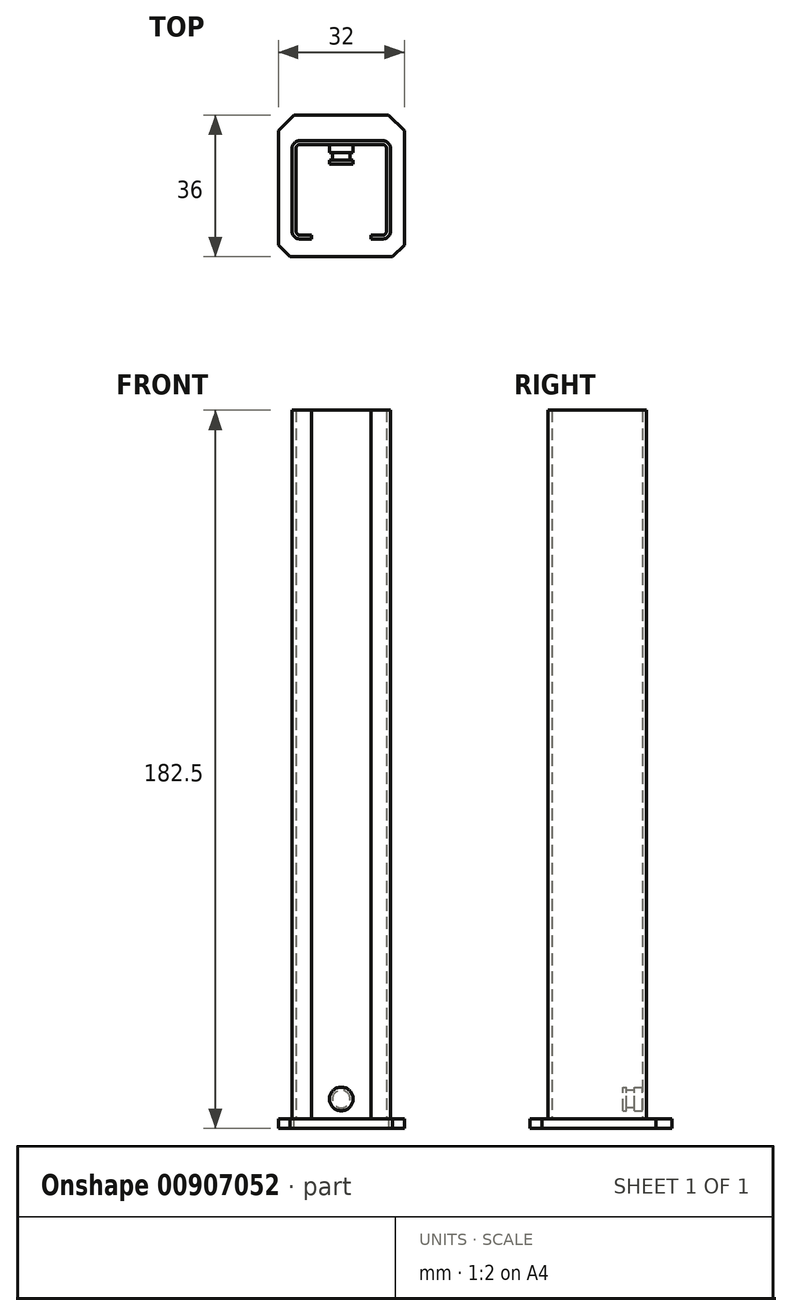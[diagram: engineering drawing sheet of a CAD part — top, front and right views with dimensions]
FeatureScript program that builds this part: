
annotation { "Feature Type Name" : "Feature", "Feature Type Description" : "" }
export const myFeature = defineFeature(function(context is Context, id is Id, definition is map)
    precondition{}
    {
        {
            var Q0;
            Q0=qCreatedBy(makeId("Top.planeOp"),FACE);
            var sketch = newSketch(context, id + "F0", { "sketchPlane" : qUnion([Q0])});
            skLineSegment(sketch, "E0.bottom", {"start": v(16, 19) * mm, "end": v(-16, 19) * mm});
            skLineSegment(sketch, "E0.top", {"start": v(16, -17) * mm, "end": v(-16, -17) * mm});
            skLineSegment(sketch, "E0.left", {"start": v(16, 19) * mm, "end": v(16, -17) * mm});
            skLineSegment(sketch, "E0.right", {"start": v(-16, 19) * mm, "end": v(-16, -17) * mm});
            skPoint(sketch, "E0.middle", {"position": v(0, 1) * mm});
            skSolve(sketch);
        }
        {
            var Q0;
            Q0 = qSketchRegion(id + "F0", true);
            extrude(context, id + "F1", {"entities" : qUnion([Q0]), "oppositeDirection" : true, "depth" : 2.5 * mm, "offsetDistance" : 25.4 * mm});
        }
        {
            var Q0;
            Q0=makeQuery(id+"F1.opExtrude","CAP_FACE",FACE,{"disambiguationData":[OSD([sQuery(id+"F0.wireOp",EDGE,"E0.bottom"),sQuery(id+"F0.wireOp",EDGE,"E0.top"),sQuery(id+"F0.wireOp",EDGE,"E0.left"),sQuery(id+"F0.wireOp",EDGE,"E0.right")])],"isStart":true});
            var sketch = newSketch(context, id + "F2", { "sketchPlane" : qUnion([Q0])});
            skLineSegment(sketch, "E1.bottom", {"start": v(12.5, 12.5) * mm, "end": v(-12.5, 12.5) * mm});
            skLineSegment(sketch, "E1.top", {"start": v(12.5, -12.5) * mm, "end": v(7.5, -12.5) * mm});
            skLineSegment(sketch, "E1.left", {"start": v(12.5, 12.5) * mm, "end": v(12.5, -12.5) * mm});
            skLineSegment(sketch, "E1.right", {"start": v(-12.5, 12.5) * mm, "end": v(-12.5, -12.5) * mm});
            skPoint(sketch, "E1.middle", {"position": v(0, 0) * mm});
            skLineSegment(sketch, "E2.0", {"start": v(11.5, 11.5) * mm, "end": v(-11.5, 11.5) * mm});
            skLineSegment(sketch, "E2.1", {"start": v(11.5, 11.5) * mm, "end": v(11.5, -11.5) * mm});
            skLineSegment(sketch, "E2.2", {"start": v(11.5, -11.5) * mm, "end": v(7.5, -11.5) * mm});
            skLineSegment(sketch, "E2.3", {"start": v(-11.5, 11.5) * mm, "end": v(-11.5, -11.5) * mm});
            skLineSegment(sketch, "E3", {"start": v(-7.5, -11.5) * mm, "end": v(-7.5, -12.5) * mm});
            skLineSegment(sketch, "E4.MirrorCS", {"start": v(7.5, -11.5) * mm, "end": v(7.5, -12.5) * mm});
            skLineSegment(sketch, "E5.trimOffspring", {"start": v(-7.5, -11.5) * mm, "end": v(-11.5, -11.5) * mm});
            skLineSegment(sketch, "E6.trimOffspring", {"start": v(-7.5, -12.5) * mm, "end": v(-12.5, -12.5) * mm});
            skSolve(sketch);
        }
        {
            var Q0;
            Q0 = qSketchRegion(id + "F2", true);
            extrude(context, id + "F3", {"entities" : qUnion([Q0]), "operationType" : NewBodyOperationType.ADD, "depth" : 180 * mm, "offsetDistance" : 25 * mm});
        }
        {
            var Q0;
            Q0=makeQuery(id+"F3.opExtrude","SWEPT_EDGE",EDGE,{"disambiguationData":[OSD([sQuery(id+"F2.wireOp",EDGE,"E2.0"),sQuery(id+"F2.wireOp",EDGE,"E2.3")])]});
            var Q1;
            Q1=makeQuery(id+"F3.opExtrude","SWEPT_EDGE",EDGE,{"disambiguationData":[OSD([sQuery(id+"F2.wireOp",EDGE,"E2.0"),sQuery(id+"F2.wireOp",EDGE,"E2.1")])]});
            var Q2;
            Q2=makeQuery(id+"F3.opExtrude","SWEPT_EDGE",EDGE,{"disambiguationData":[OSD([sQuery(id+"F2.wireOp",EDGE,"E2.3"),sQuery(id+"F2.wireOp",EDGE,"E5.trimOffspring")])]});
            var Q3;
            Q3=makeQuery(id+"F3.opExtrude","SWEPT_EDGE",EDGE,{"disambiguationData":[OSD([sQuery(id+"F2.wireOp",EDGE,"E2.1"),sQuery(id+"F2.wireOp",EDGE,"E2.2")])]});
            fillet(context, id + "F4", {"entities" : qUnion([Q0, Q1, Q2, Q3]), "radius" : 1 * mm, "tangentPropagation" : true, "allowEdgeOverflow" : false});
        }
        {
            var Q0;
            Q0=makeQuery(id+"F3.opExtrude","SWEPT_EDGE",EDGE,{"disambiguationData":[OSD([sQuery(id+"F2.wireOp",EDGE,"E1.bottom"),sQuery(id+"F2.wireOp",EDGE,"E1.right")])]});
            var Q1;
            Q1=makeQuery(id+"F3.opExtrude","SWEPT_EDGE",EDGE,{"disambiguationData":[OSD([sQuery(id+"F2.wireOp",EDGE,"E1.bottom"),sQuery(id+"F2.wireOp",EDGE,"E1.left")])]});
            var Q2;
            Q2=makeQuery(id+"F3.opExtrude","SWEPT_EDGE",EDGE,{"disambiguationData":[OSD([sQuery(id+"F2.wireOp",EDGE,"E1.top"),sQuery(id+"F2.wireOp",EDGE,"E1.left")])]});
            var Q3;
            Q3=makeQuery(id+"F3.opExtrude","SWEPT_EDGE",EDGE,{"disambiguationData":[OSD([sQuery(id+"F2.wireOp",EDGE,"E1.right"),sQuery(id+"F2.wireOp",EDGE,"E6.trimOffspring")])]});
            fillet(context, id + "F5", {"entities" : qUnion([Q0, Q1, Q2, Q3]), "radius" : 2 * mm, "tangentPropagation" : true, "allowEdgeOverflow" : false});
        }
        {
            var Q0;
            Q0=makeQuery(id+"F3.opExtrude","SWEPT_FACE",FACE,{"disambiguationData":[OSD([sQuery(id+"F2.wireOp",EDGE,"E2.0")])]});
            var sketch = newSketch(context, id + "F6", { "sketchPlane" : qUnion([Q0])});
            skCircle(sketch, "E7", {"center": v(0, 5) * mm, "radius": 3 * mm});
            skSolve(sketch);
        }
        {
            var Q0;
            Q0 = qSketchRegion(id + "F6", true);
            extrude(context, id + "F7", {"entities" : qUnion([Q0]), "operationType" : NewBodyOperationType.ADD, "depth" : 5 * mm, "offsetDistance" : 25 * mm});
        }
        {
            var Q0;
            Q0=makeQuery(id+"F3.opExtrude","SWEPT_FACE",FACE,{"disambiguationData":[OSD([sQuery(id+"F2.wireOp",EDGE,"E2.0")])]});
            cPlane(context, id + "F8", {"entities" : qUnion([Q0]), "cplaneType" : CPlaneType.OFFSET, "offset" : 3 * mm, "width" : 150 * mm, "height" : 150 * mm});
        }
        {
            var Q0;
            Q0=qCreatedBy(id+"F8.planeOp",FACE);
            var sketch = newSketch(context, id + "F9", { "sketchPlane" : qUnion([Q0])});
            skCircle(sketch, "E8.0", {"center": v(0, 5) * mm, "radius": 3 * mm});
            skCircle(sketch, "E9", {"center": v(0, 5) * mm, "radius": 2.25 * mm});
            skSolve(sketch);
        }
        {
            var Q0;
            Q0 = qSketchRegion(id + "F9", true);
            extrude(context, id + "F10", {"entities" : qUnion([Q0]), "operationType" : NewBodyOperationType.REMOVE, "endBound" : BoundingType.SYMMETRIC, "oppositeDirection" : true, "depth" : 2 * mm, "offsetDistance" : 25 * mm});
        }
        {
            var Q0;
            Q0=makeQuery(id+"F1.opExtrude","SWEPT_EDGE",EDGE,{"disambiguationData":[OSD([sQuery(id+"F0.wireOp",EDGE,"E0.top"),sQuery(id+"F0.wireOp",EDGE,"E0.right")])]});
            var Q1;
            Q1=makeQuery(id+"F1.opExtrude","SWEPT_EDGE",EDGE,{"disambiguationData":[OSD([sQuery(id+"F0.wireOp",EDGE,"E0.top"),sQuery(id+"F0.wireOp",EDGE,"E0.left")])]});
            chamfer(context, id + "F11", {"entities" : qUnion([Q0, Q1]), "width" : 3 * mm, "tangentPropagation" : true});
        }
        {
            var Q0;
            Q0=makeQuery(id+"F1.opExtrude","SWEPT_EDGE",EDGE,{"disambiguationData":[OSD([sQuery(id+"F0.wireOp",EDGE,"E0.bottom"),sQuery(id+"F0.wireOp",EDGE,"E0.left")])]});
            var Q1;
            Q1=makeQuery(id+"F1.opExtrude","SWEPT_EDGE",EDGE,{"disambiguationData":[OSD([sQuery(id+"F0.wireOp",EDGE,"E0.bottom"),sQuery(id+"F0.wireOp",EDGE,"E0.right")])]});
            chamfer(context, id + "F12", {"entities" : qUnion([Q0, Q1]), "width" : 4 * mm, "tangentPropagation" : true});
        }
    });
